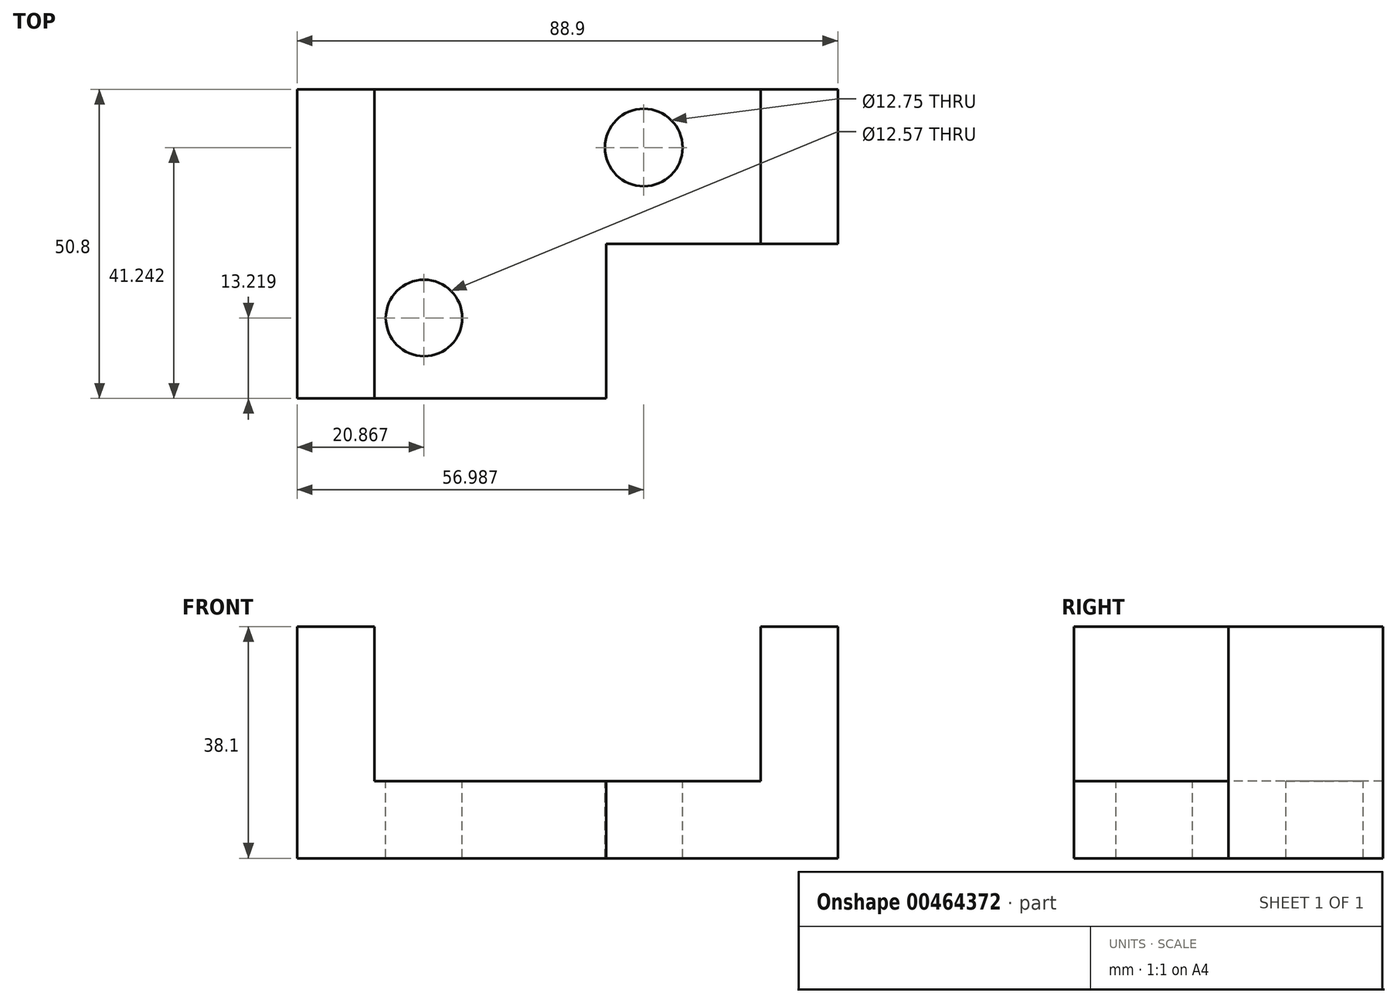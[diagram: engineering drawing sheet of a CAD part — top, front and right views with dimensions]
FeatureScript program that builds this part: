
annotation { "Feature Type Name" : "Feature", "Feature Type Description" : "" }
export const myFeature = defineFeature(function(context is Context, id is Id, definition is map)
    precondition{}
    {
        {
            var Q0;
            Q0=qCreatedBy(makeId("Front.planeOp"),FACE);
            var sketch = newSketch(context, id + "F0", { "sketchPlane" : qUnion([Q0])});
            skLineSegment(sketch, "E0.bottom", {"start": v(-42.8, 2.81) * mm, "end": v(46.1, 2.81) * mm});
            skLineSegment(sketch, "E0.top", {"start": v(-42.8, -35.29) * mm, "end": v(46.1, -35.29) * mm});
            skLineSegment(sketch, "E0.left", {"start": v(-42.8, 2.81) * mm, "end": v(-42.8, -35.29) * mm});
            skLineSegment(sketch, "E0.right", {"start": v(46.1, 2.81) * mm, "end": v(46.1, -35.29) * mm});
            skSolve(sketch);
        }
        {
            var Q0;
            Q0 = qSketchRegion(id + "F0", true);
            extrude(context, id + "F1", {"entities" : qUnion([Q0]), "depth" : 50.8 * mm});
        }
        {
            var Q0;
            Q0=makeQuery(id+"F1.opExtrude","CAP_FACE",FACE,{"disambiguationData":[OSD([sQuery(id+"F0.wireOp",EDGE,"E0.bottom"),sQuery(id+"F0.wireOp",EDGE,"E0.top"),sQuery(id+"F0.wireOp",EDGE,"E0.left"),sQuery(id+"F0.wireOp",EDGE,"E0.right")])],"isStart":false});
            var sketch = newSketch(context, id + "F2", { "sketchPlane" : qUnion([Q0])});
            skLineSegment(sketch, "E1.bottom", {"start": v(-30.1, 2.81) * mm, "end": v(33.4, 2.81) * mm});
            skLineSegment(sketch, "E1.top", {"start": v(-30.1, -22.59) * mm, "end": v(33.4, -22.59) * mm});
            skLineSegment(sketch, "E1.left", {"start": v(-30.1, 2.81) * mm, "end": v(-30.1, -22.59) * mm});
            skLineSegment(sketch, "E1.right", {"start": v(33.4, 2.81) * mm, "end": v(33.4, -22.59) * mm});
            skSolve(sketch);
        }
        {
            var Q0;
            Q0 = qSketchRegion(id + "F2", true);
            extrude(context, id + "F3", {"entities" : qUnion([Q0]), "operationType" : NewBodyOperationType.REMOVE, "oppositeDirection" : true, "depth" : 50.8 * mm});
        }
        {
            var Q0;
            Q0=makeQuery(id+"F3.boolean.opBoolean","COPY",FACE,{"derivedFrom":makeQuery(id+"F3.opExtrude","SWEPT_FACE",FACE,{"disambiguationData":[OSD([sQuery(id+"F2.wireOp",EDGE,"E1.top")])]})});
            var sketch = newSketch(context, id + "F4", { "sketchPlane" : qUnion([Q0])});
            skLineSegment(sketch, "E2.bottom", {"start": v(46.1, -25.4) * mm, "end": v(8, -25.4) * mm});
            skLineSegment(sketch, "E2.top", {"start": v(46.1, -50.8) * mm, "end": v(8, -50.8) * mm});
            skLineSegment(sketch, "E2.left", {"start": v(46.1, -25.4) * mm, "end": v(46.1, -50.8) * mm});
            skLineSegment(sketch, "E2.right", {"start": v(8, -25.4) * mm, "end": v(8, -50.8) * mm});
            skSolve(sketch);
        }
        {
            var Q0;
            Q0 = qSketchRegion(id + "F4", true);
            extrude(context, id + "F5", {"entities" : qUnion([Q0]), "operationType" : NewBodyOperationType.REMOVE, "oppositeDirection" : true, "depth" : 38.1 * mm});
        }
        {
            var Q0;
            {var subQ0=sQuery(id+"F0.wireOp",EDGE,"E0.right");var subQ3=sQuery(id+"F0.wireOp",EDGE,"E0.bottom");Q0=makeQuery(id+"F3.boolean.opBoolean","SPLIT",FACE,{"disambiguationData":[TD([makeQuery(id+"F1.opExtrude","SWEPT_FACE",FACE,{"disambiguationData":[OSD([subQ0])]})])],"derivedFrom":makeQuery(id+"F1.opExtrude","SWEPT_FACE",FACE,{"disambiguationData":[OSD([subQ3])]})});}
            var sketch = newSketch(context, id + "F6", { "sketchPlane" : qUnion([Q0])});
            skLineSegment(sketch, "E3.bottom", {"start": v(33.4, -25.4) * mm, "end": v(46.1, -25.4) * mm});
            skLineSegment(sketch, "E3.top", {"start": v(33.4, -50.8) * mm, "end": v(46.1, -50.8) * mm});
            skLineSegment(sketch, "E3.left", {"start": v(33.4, -25.4) * mm, "end": v(33.4, -50.8) * mm});
            skLineSegment(sketch, "E3.right", {"start": v(46.1, -25.4) * mm, "end": v(46.1, -50.8) * mm});
            skSolve(sketch);
        }
        {
            var Q0;
            Q0 = qSketchRegion(id + "F6", true);
            extrude(context, id + "F7", {"entities" : qUnion([Q0]), "operationType" : NewBodyOperationType.REMOVE, "oppositeDirection" : true, "depth" : 38.1 * mm});
        }
        {
            var Q0;
            Q0=makeQuery(id+"F3.boolean.opBoolean","COPY",FACE,{"derivedFrom":makeQuery(id+"F3.opExtrude","SWEPT_FACE",FACE,{"disambiguationData":[OSD([sQuery(id+"F2.wireOp",EDGE,"E1.top")])]})});
            var sketch = newSketch(context, id + "F8", { "sketchPlane" : qUnion([Q0])});
            skCircle(sketch, "E4", {"center": v(14.19, -9.56) * mm, "radius": 6.37 * mm});
            skSolve(sketch);
        }
        {
            var Q0;
            Q0=makeQuery(id+"F8.imprint","IMPRINT",FACE,{"disambiguationData":[TD([[makeQuery(id+"F8.imprint","IMPRINT",EDGE,{"derivedFrom":sQuery(id+"F8.wireOp",EDGE,"E4")}),1.0]])]});
            extrude(context, id + "F9", {"entities" : qUnion([Q0]), "operationType" : NewBodyOperationType.REMOVE, "oppositeDirection" : true, "depth" : 25.4 * mm});
        }
        {
            var Q0;
            Q0=makeQuery(id+"F3.boolean.opBoolean","COPY",FACE,{"derivedFrom":makeQuery(id+"F3.opExtrude","SWEPT_FACE",FACE,{"disambiguationData":[OSD([sQuery(id+"F2.wireOp",EDGE,"E1.top")])]})});
            var sketch = newSketch(context, id + "F10", { "sketchPlane" : qUnion([Q0])});
            skCircle(sketch, "E5", {"center": v(-21.93, -37.58) * mm, "radius": 6.28 * mm});
            skSolve(sketch);
        }
        {
            var Q0;
            Q0 = qSketchRegion(id + "F10", true);
            extrude(context, id + "F11", {"entities" : qUnion([Q0]), "operationType" : NewBodyOperationType.REMOVE, "oppositeDirection" : true, "depth" : 25.4 * mm});
        }
    });
